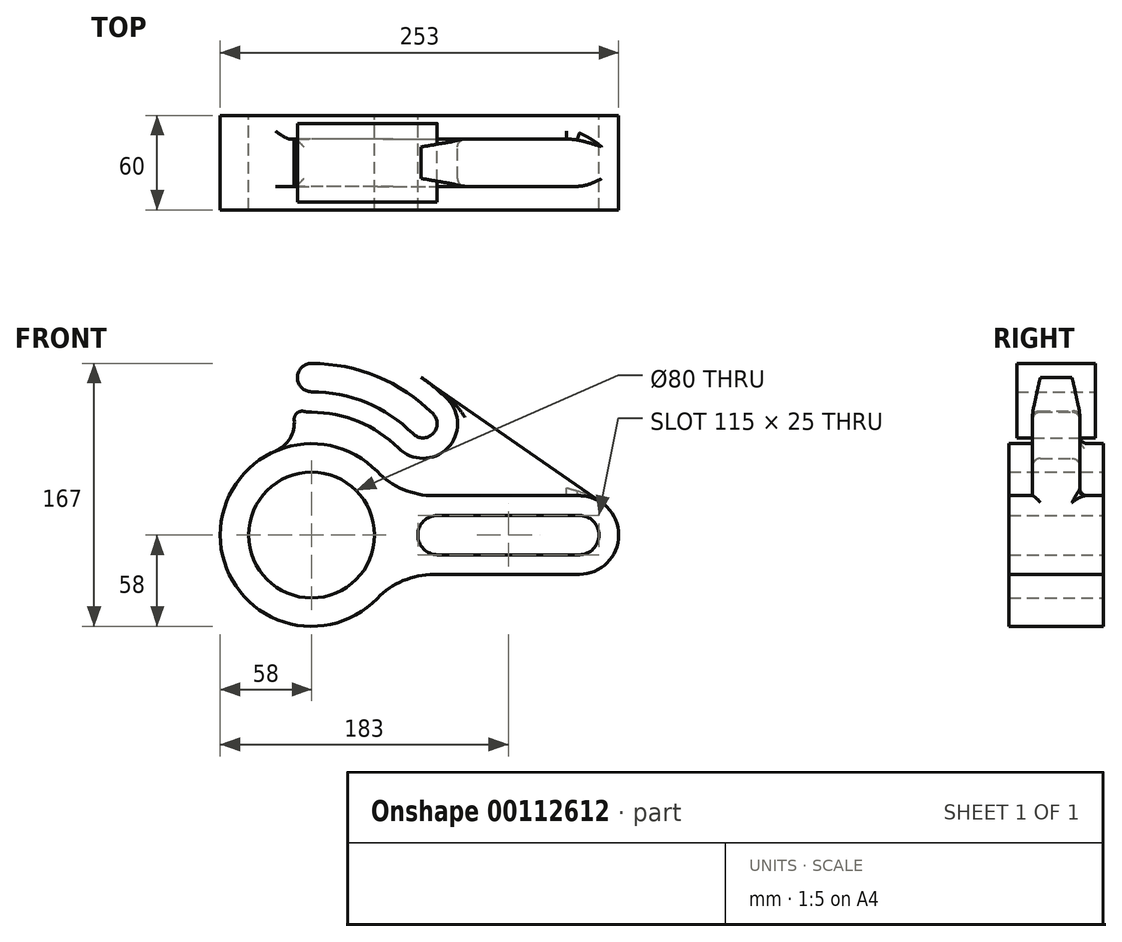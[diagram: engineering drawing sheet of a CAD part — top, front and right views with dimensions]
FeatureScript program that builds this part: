
annotation { "Feature Type Name" : "Feature", "Feature Type Description" : "" }
export const myFeature = defineFeature(function(context is Context, id is Id, definition is map)
    precondition{}
    {
        {
            var Q0;
            Q0=qCreatedBy(makeId("Front.planeOp"),FACE);
            var sketch = newSketch(context, id + "F0", { "sketchPlane" : qUnion([Q0])});
            skCircle(sketch, "E0", {"center": v(0, 0) * mm, "radius": 40 * mm});
            skLineSegment(sketch, "E1", {"start": v(80, 0) * mm, "end": v(170, 0) * mm, "construction": true});
            skArc(sketch, "E2.0", {"start": v(0, 100) * mm, "mid": v(38.27, 92.39) * mm, "end": v(70.71, 70.71) * mm, "construction": true});
            skArc(sketch, "E3.0.startCap", {"start": v(0, 91) * mm, "mid": v(-9, 100) * mm, "end": v(0, 109) * mm});
            skArc(sketch, "E3.0.endCap", {"start": v(77.07, 77.07) * mm, "mid": v(77.07, 64.35) * mm, "end": v(64.35, 64.35) * mm});
            skArc(sketch, "E3.0.left", {"start": v(0, 109) * mm, "mid": v(41.71, 100.7) * mm, "end": v(77.07, 77.07) * mm});
            skArc(sketch, "E3.0.right", {"start": v(0, 91) * mm, "mid": v(34.82, 84.07) * mm, "end": v(64.35, 64.35) * mm});
            skArc(sketch, "E4.0.endCap", {"start": v(170, 25) * mm, "mid": v(195, 0) * mm, "end": v(170, -25) * mm});
            skLineSegment(sketch, "E4.0.left", {"start": v(77.71, 25) * mm, "end": v(170, 25) * mm});
            skLineSegment(sketch, "E4.0.right", {"start": v(77.71, -25) * mm, "end": v(170, -25) * mm});
            skArc(sketch, "E5.0.startCap", {"start": v(0, 78) * mm, "mid": v(-22, 100) * mm, "end": v(0, 122) * mm});
            skArc(sketch, "E5.0.endCap", {"start": v(86.27, 86.27) * mm, "mid": v(86.27, 55.15) * mm, "end": v(55.15, 55.15) * mm});
            skArc(sketch, "E5.0.left", {"start": v(0, 122) * mm, "mid": v(46.69, 112.71) * mm, "end": v(86.27, 86.27) * mm});
            skArc(sketch, "E5.0.right", {"start": v(0, 78) * mm, "mid": v(29.85, 72.06) * mm, "end": v(55.15, 55.15) * mm});
            skArc(sketch, "E6.0.startCap", {"start": v(80, -12.5) * mm, "mid": v(67.5, 0) * mm, "end": v(80, 12.5) * mm});
            skArc(sketch, "E6.0.endCap", {"start": v(170, 12.5) * mm, "mid": v(182.5, 0) * mm, "end": v(170, -12.5) * mm});
            skLineSegment(sketch, "E6.0.left", {"start": v(80, 12.5) * mm, "end": v(170, 12.5) * mm});
            skLineSegment(sketch, "E6.0.right", {"start": v(80, -12.5) * mm, "end": v(170, -12.5) * mm});
            skLineSegment(sketch, "E7", {"start": v(184.26, 20.53) * mm, "end": v(69.61, 100.2) * mm});
            skArc(sketch, "E8", {"start": v(41.73, -40.28) * mm, "mid": v(-58, 0) * mm, "end": v(41.73, 40.28) * mm});
            skArc(sketch, "E9", {"start": v(77.71, -25) * mm, "mid": v(58.17, -28.98) * mm, "end": v(41.73, -40.28) * mm});
            skArc(sketch, "E10", {"start": v(41.73, 40.28) * mm, "mid": v(58.17, 28.98) * mm, "end": v(77.71, 25) * mm});
            skArc(sketch, "E11", {"start": v(-23, 53.24) * mm, "mid": v(-11.38, 67.43) * mm, "end": v(-16.2, 85.12) * mm});
            skLineSegment(sketch, "E12", {"start": v(0, 0) * mm, "end": v(117.68, 117.68) * mm, "construction": true});
            skSolve(sketch);
        }
        {
            var Q0;
            Q0=makeQuery(id+"F0.imprint","IMPRINT",FACE,{"disambiguationData":[TD([[makeQuery(id+"F0.imprint","IMPRINT",EDGE,{"derivedFrom":sQuery(id+"F0.wireOp",EDGE,"E0")}),-1.0]])]});
            extrude(context, id + "F1", {"entities" : qUnion([Q0]), "endBound" : BoundingType.SYMMETRIC, "depth" : 60 * mm});
        }
        {
            var Q0;
            Q0=makeQuery(id+"F0.imprint","IMPRINT",FACE,{"disambiguationData":[TD([[makeQuery(id+"F0.imprint","IMPRINT",EDGE,{"derivedFrom":sQuery(id+"F0.wireOp",EDGE,"E3.0.startCap")}),1.0]])]});
            extrude(context, id + "F2", {"entities" : qUnion([Q0]), "operationType" : NewBodyOperationType.ADD, "endBound" : BoundingType.SYMMETRIC, "depth" : 50 * mm});
        }
        {
            var Q0;
            {var subQ5=sQuery(id+"F0.wireOp",EDGE,"E4.0.left");Q0=makeQuery(id+"F0.imprint","IMPRINT",FACE,{"disambiguationData":[TD([[makeQuery(id+"F0.imprint","IMPRINT",EDGE,{"derivedFrom":subQ5}),1.0]])]});}
            extrude(context, id + "F3", {"entities" : qUnion([Q0]), "operationType" : NewBodyOperationType.ADD, "endBound" : BoundingType.SYMMETRIC, "depth" : 30 * mm});
        }
        {
            var Q0;
            Q0=makeQuery(id+"F3.opExtrude","CAP_EDGE",EDGE,{"disambiguationData":[OSD([sQuery(id+"F0.wireOp",EDGE,"E7")])],"isStart":false});
            var Q1;
            Q1=makeQuery(id+"F3.opExtrude","CAP_EDGE",EDGE,{"disambiguationData":[OSD([sQuery(id+"F0.wireOp",EDGE,"E7")])],"isStart":true});
            var Q2;
            Q2=makeQuery(id+"F3.opExtrude","CAP_EDGE",EDGE,{"disambiguationData":[OSD([sQuery(id+"F0.wireOp",EDGE,"E10")])],"isStart":false});
            var Q3;
            Q3=makeQuery(id+"F3.opExtrude","CAP_EDGE",EDGE,{"disambiguationData":[OSD([sQuery(id+"F0.wireOp",EDGE,"E8")])],"isStart":false});
            var Q4;
            Q4=makeQuery(id+"F3.opExtrude","CAP_EDGE",EDGE,{"disambiguationData":[OSD([sQuery(id+"F0.wireOp",EDGE,"E4.0.left")])],"isStart":false});
            var Q5;
            Q5=makeQuery(id+"F3.opExtrude","CAP_EDGE",EDGE,{"disambiguationData":[OSD([sQuery(id+"F0.wireOp",EDGE,"E4.0.endCap")])],"isStart":false});
            var Q6;
            Q6=makeQuery(id+"F3.opExtrude","CAP_EDGE",EDGE,{"disambiguationData":[OSD([sQuery(id+"F0.wireOp",EDGE,"E4.0.endCap")])],"isStart":true});
            var Q7;
            Q7=makeQuery(id+"F3.opExtrude","CAP_EDGE",EDGE,{"disambiguationData":[OSD([sQuery(id+"F0.wireOp",EDGE,"E4.0.left")])],"isStart":true});
            var Q8;
            Q8=makeQuery(id+"F3.opExtrude","CAP_EDGE",EDGE,{"disambiguationData":[OSD([sQuery(id+"F0.wireOp",EDGE,"E8")])],"isStart":true});
            var Q9;
            Q9=makeQuery(id+"F3.opExtrude","CAP_EDGE",EDGE,{"disambiguationData":[OSD([sQuery(id+"F0.wireOp",EDGE,"E10")])],"isStart":true});
            var Q10;
            Q10=makeQuery(id+"F3.opExtrude","CAP_EDGE",EDGE,{"disambiguationData":[OSD([sQuery(id+"F0.wireOp",EDGE,"E5.0.endCap")])],"isStart":true});
            var Q11;
            Q11=makeQuery(id+"F3.opExtrude","CAP_EDGE",EDGE,{"disambiguationData":[OSD([sQuery(id+"F0.wireOp",EDGE,"E5.0.left")])],"isStart":true});
            var Q12;
            Q12=makeQuery(id+"F3.opExtrude","CAP_EDGE",EDGE,{"disambiguationData":[OSD([sQuery(id+"F0.wireOp",EDGE,"E5.0.right")])],"isStart":true});
            var Q13;
            Q13=makeQuery(id+"F3.opExtrude","CAP_EDGE",EDGE,{"disambiguationData":[OSD([sQuery(id+"F0.wireOp",EDGE,"E5.0.startCap")])],"isStart":true});
            var Q14;
            Q14=makeQuery(id+"F3.opExtrude","CAP_EDGE",EDGE,{"disambiguationData":[OSD([sQuery(id+"F0.wireOp",EDGE,"E5.0.startCap")])],"isStart":false});
            var Q15;
            Q15=makeQuery(id+"F3.opExtrude","CAP_EDGE",EDGE,{"disambiguationData":[OSD([sQuery(id+"F0.wireOp",EDGE,"E5.0.right")])],"isStart":false});
            var Q16;
            Q16=makeQuery(id+"F3.opExtrude","CAP_EDGE",EDGE,{"disambiguationData":[OSD([sQuery(id+"F0.wireOp",EDGE,"E5.0.endCap")])],"isStart":false});
            var Q17;
            Q17=makeQuery(id+"F3.opExtrude","SWEPT_EDGE",EDGE,{"disambiguationData":[OSD([sQuery(id+"F0.wireOp",EDGE,"E5.0.startCap"),sQuery(id+"F0.wireOp",EDGE,"E11")])]});
            var Q18;
            Q18=makeQuery(id+"F3.opExtrude","SWEPT_EDGE",EDGE,{"disambiguationData":[OSD([sQuery(id+"F0.wireOp",EDGE,"E8"),sQuery(id+"F0.wireOp",EDGE,"E11")])]});
            fillet(context, id + "F4", {"entities" : qUnion([Q0, Q1, Q2, Q3, Q4, Q5, Q6, Q7, Q8, Q9, Q10, Q11, Q12, Q13, Q14, Q15, Q16, Q17, Q18]), "radius" : 5 * mm, "tangentPropagation" : true, "allowEdgeOverflow" : false});
        }
    });
